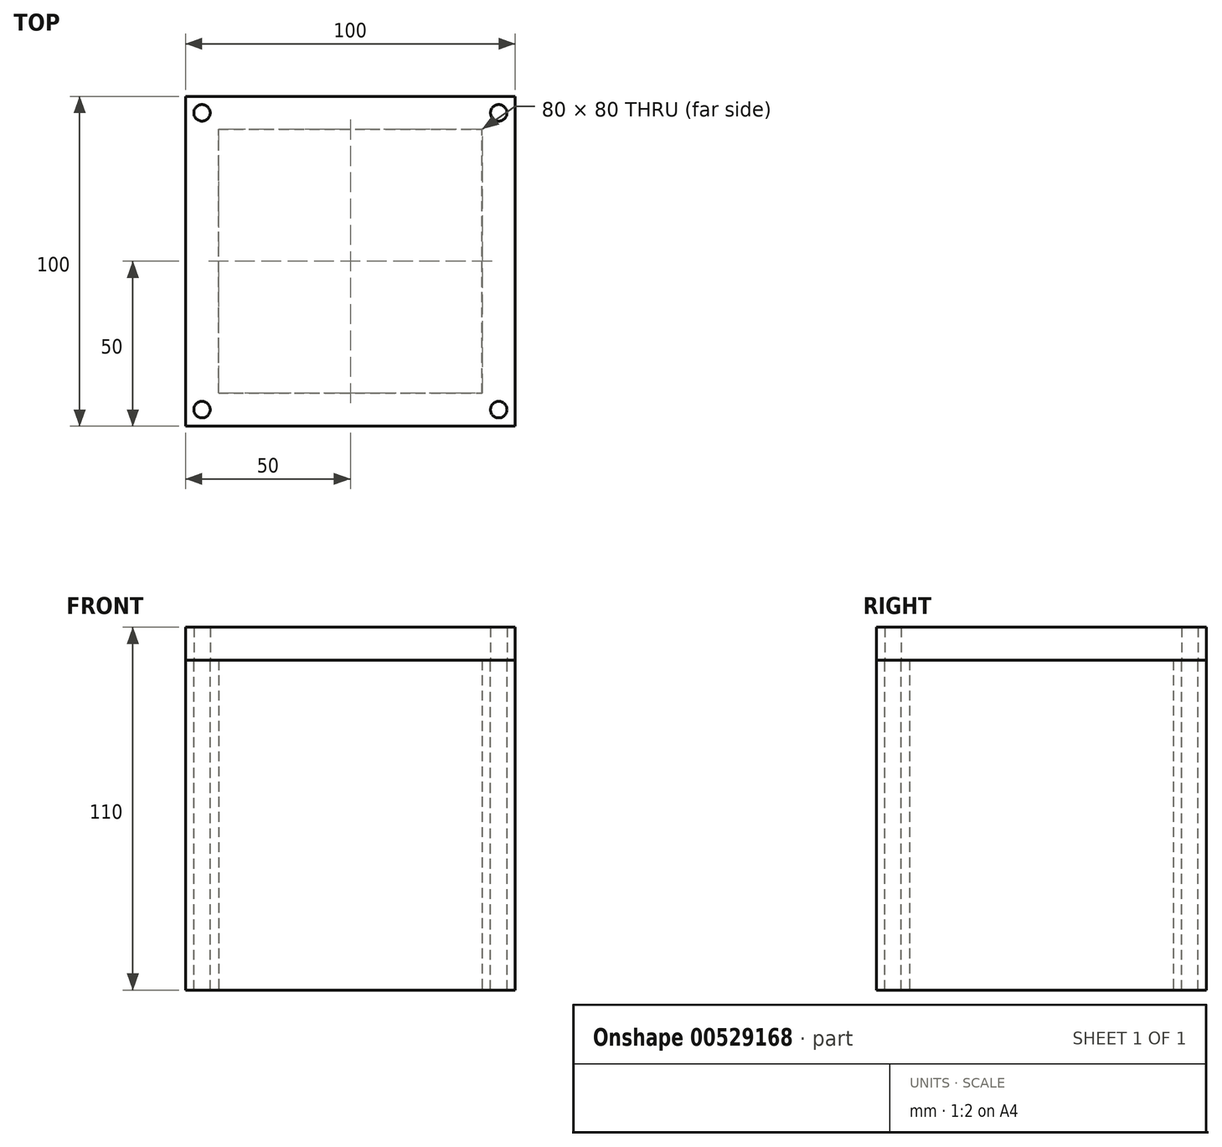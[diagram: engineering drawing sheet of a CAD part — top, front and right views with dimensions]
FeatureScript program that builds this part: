
annotation { "Feature Type Name" : "Feature", "Feature Type Description" : "" }
export const myFeature = defineFeature(function(context is Context, id is Id, definition is map)
    precondition{}
    {
        {
            var Q0;
            Q0=qCreatedBy(makeId("Top.planeOp"),FACE);
            var sketch = newSketch(context, id + "F0", { "sketchPlane" : qUnion([Q0])});
            skLineSegment(sketch, "E0.bottom", {"start": v(0, 0) * mm, "end": v(100, 0) * mm});
            skLineSegment(sketch, "E0.top", {"start": v(0, 100) * mm, "end": v(100, 100) * mm});
            skLineSegment(sketch, "E0.left", {"start": v(0, 0) * mm, "end": v(0, 100) * mm});
            skLineSegment(sketch, "E0.right", {"start": v(100, 0) * mm, "end": v(100, 100) * mm});
            skLineSegment(sketch, "E1.0", {"start": v(10, 90) * mm, "end": v(90, 90) * mm});
            skLineSegment(sketch, "E1.1", {"start": v(10, 10) * mm, "end": v(10, 90) * mm});
            skLineSegment(sketch, "E1.2", {"start": v(10, 10) * mm, "end": v(90, 10) * mm});
            skLineSegment(sketch, "E1.3", {"start": v(90, 10) * mm, "end": v(90, 90) * mm});
            skSolve(sketch);
        }
        {
            var Q0;
            Q0 = qSketchRegion(id + "F0", true);
            extrude(context, id + "F1", {"entities" : qUnion([Q0]), "depth" : 100 * mm, "offsetDistance" : 25 * mm});
        }
        {
            var Q0;
            Q0=makeQuery(id+"F1.opExtrude","CAP_FACE",FACE,{"disambiguationData":[OSD([sQuery(id+"F0.wireOp",EDGE,"E0.bottom"),sQuery(id+"F0.wireOp",EDGE,"E0.top"),sQuery(id+"F0.wireOp",EDGE,"E0.left"),sQuery(id+"F0.wireOp",EDGE,"E0.right"),sQuery(id+"F0.wireOp",EDGE,"E1.0"),sQuery(id+"F0.wireOp",EDGE,"E1.1"),sQuery(id+"F0.wireOp",EDGE,"E1.2"),sQuery(id+"F0.wireOp",EDGE,"E1.3")])],"isStart":false});
            var sketch = newSketch(context, id + "F2", { "sketchPlane" : qUnion([Q0])});
            skCircle(sketch, "E2", {"center": v(5, 95) * mm, "radius": 2.5 * mm});
            skLineSegment(sketch, "E3", {"start": v(50, 100) * mm, "end": v(50, 0) * mm, "construction": true});
            skLineSegment(sketch, "E4", {"start": v(0, 50) * mm, "end": v(100, 50) * mm, "construction": true});
            skCircle(sketch, "E5.MirrorC", {"center": v(95, 95) * mm, "radius": 2.5 * mm});
            skCircle(sketch, "E6.MirrorC", {"center": v(5, 5) * mm, "radius": 2.5 * mm});
            skCircle(sketch, "E7.MirrorC", {"center": v(95, 5) * mm, "radius": 2.5 * mm});
            skSolve(sketch);
        }
        {
            var Q0;
            Q0 = qSketchRegion(id + "F2", true);
            extrude(context, id + "F3", {"entities" : qUnion([Q0]), "operationType" : NewBodyOperationType.REMOVE, "endBound" : BoundingType.THROUGH_ALL, "oppositeDirection" : true, "depth" : 25 * mm, "offsetDistance" : 25 * mm});
        }
        {
            var Q0;
            Q0=makeQuery(id+"F1.opExtrude","CAP_FACE",FACE,{"disambiguationData":[OSD([sQuery(id+"F0.wireOp",EDGE,"E0.bottom"),sQuery(id+"F0.wireOp",EDGE,"E0.top"),sQuery(id+"F0.wireOp",EDGE,"E0.left"),sQuery(id+"F0.wireOp",EDGE,"E0.right"),sQuery(id+"F0.wireOp",EDGE,"E1.0"),sQuery(id+"F0.wireOp",EDGE,"E1.1"),sQuery(id+"F0.wireOp",EDGE,"E1.2"),sQuery(id+"F0.wireOp",EDGE,"E1.3")])],"isStart":false});
            var sketch = newSketch(context, id + "F4", { "sketchPlane" : qUnion([Q0])});
            skLineSegment(sketch, "E8.bottom", {"start": v(0, 0) * mm, "end": v(100, 0) * mm});
            skLineSegment(sketch, "E8.top", {"start": v(0, 100) * mm, "end": v(100, 100) * mm});
            skLineSegment(sketch, "E8.left", {"start": v(0, 0) * mm, "end": v(0, 100) * mm});
            skLineSegment(sketch, "E8.right", {"start": v(100, 0) * mm, "end": v(100, 100) * mm});
            skCircle(sketch, "E9.0", {"center": v(5, 5) * mm, "radius": 2.5 * mm});
            skCircle(sketch, "E10.0", {"center": v(95, 5) * mm, "radius": 2.5 * mm});
            skCircle(sketch, "E11.0", {"center": v(95, 95) * mm, "radius": 2.5 * mm});
            skCircle(sketch, "E12.0", {"center": v(5, 95) * mm, "radius": 2.5 * mm});
            skSolve(sketch);
        }
        {
            var Q0;
            Q0 = qSketchRegion(id + "F4", true);
            extrude(context, id + "F5", {"entities" : qUnion([Q0]), "depth" : 10 * mm, "offsetDistance" : 25 * mm});
        }
    });
